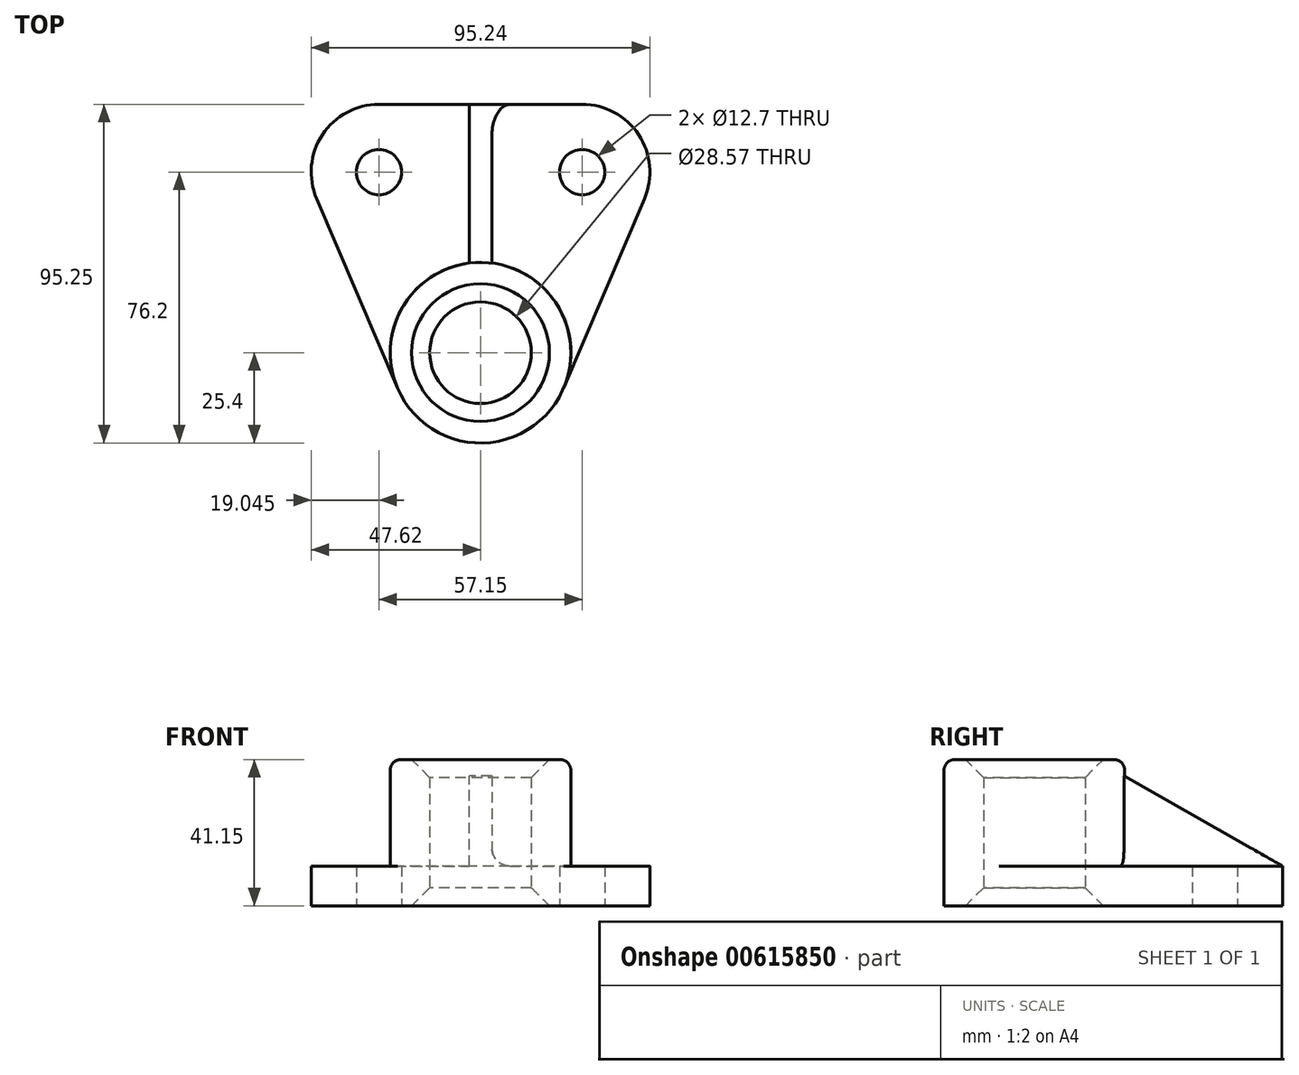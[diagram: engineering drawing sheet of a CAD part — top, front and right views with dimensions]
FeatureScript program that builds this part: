
annotation { "Feature Type Name" : "Feature", "Feature Type Description" : "" }
export const myFeature = defineFeature(function(context is Context, id is Id, definition is map)
    precondition{}
    {
        {
            var Q0;
            Q0=qCreatedBy(makeId("Top.planeOp"),FACE);
            var sketch = newSketch(context, id + "F0", { "sketchPlane" : qUnion([Q0])});
            skCircle(sketch, "E0", {"center": v(0, 0) * mm, "radius": 25.4 * mm});
            skLineSegment(sketch, "E1", {"start": v(0, 33.34) * mm, "end": v(0, -75.81) * mm, "construction": true});
            skCircle(sketch, "E2", {"center": v(0, 0) * mm, "radius": 14.29 * mm});
            skSolve(sketch);
        }
        {
            var Q0;
            Q0 = qSketchRegion(id + "F0", true);
            extrude(context, id + "F1", {"entities" : qUnion([Q0]), "depth" : 41.15 * mm, "offsetDistance" : 25.4 * mm});
        }
        {
            var Q0;
            Q0=makeQuery(id+"F1.opExtrude","CAP_FACE",FACE,{"disambiguationData":[OSD([sQuery(id+"F0.wireOp",EDGE,"E0"),sQuery(id+"F0.wireOp",EDGE,"E2")])],"isStart":true});
            var sketch = newSketch(context, id + "F2", { "sketchPlane" : qUnion([Q0])});
            skLineSegment(sketch, "E3", {"start": v(0, 41.82) * mm, "end": v(0, -91.73) * mm, "construction": true});
            skLineSegment(sketch, "E4", {"start": v(-52.73, -50.8) * mm, "end": v(63.33, -50.8) * mm, "construction": true});
            skArc(sketch, "E5", {"start": v(-46.1, -43.33) * mm, "mid": v(-44.47, -61.3) * mm, "end": v(-28.57, -69.85) * mm});
            skArc(sketch, "E6.MirrorC", {"start": v(46.1, -43.33) * mm, "mid": v(44.47, -61.3) * mm, "end": v(28.58, -69.85) * mm});
            skLineSegment(sketch, "E7", {"start": v(-52.6, 0) * mm, "end": v(62.29, 0) * mm, "construction": true});
            skCircle(sketch, "E8", {"center": v(-28.57, -50.8) * mm, "radius": 6.35 * mm});
            skCircle(sketch, "E9", {"center": v(28.58, -50.8) * mm, "radius": 6.35 * mm});
            skArc(sketch, "E10", {"start": v(-23.36, 9.97) * mm, "mid": v(0, -25.4) * mm, "end": v(23.36, 9.97) * mm});
            skLineSegment(sketch, "E11", {"start": v(-46.1, -43.33) * mm, "end": v(-23.36, 9.97) * mm});
            skLineSegment(sketch, "E12", {"start": v(23.36, 9.97) * mm, "end": v(46.1, -43.33) * mm});
            skLineSegment(sketch, "E13", {"start": v(-28.57, -69.85) * mm, "end": v(28.58, -69.85) * mm});
            skPoint(sketch, "E14.orphan", {"position": v(-52.73, -58.88) * mm});
            skSolve(sketch);
        }
        {
            var Q0;
            Q0 = qSketchRegion(id + "F2", true);
            extrude(context, id + "F3", {"entities" : qUnion([Q0]), "operationType" : NewBodyOperationType.ADD, "oppositeDirection" : true, "depth" : 11.18 * mm, "offsetDistance" : 25.4 * mm});
        }
        {
            var Q0;
            Q0=makeQuery(id+"F3.opExtrude","CAP_FACE",FACE,{"disambiguationData":[OSD([sQuery(id+"F2.wireOp",EDGE,"E5"),sQuery(id+"F2.wireOp",EDGE,"E6.MirrorC"),sQuery(id+"F2.wireOp",EDGE,"E8"),sQuery(id+"F2.wireOp",EDGE,"E9"),sQuery(id+"F2.wireOp",EDGE,"E10"),sQuery(id+"F2.wireOp",EDGE,"E11"),sQuery(id+"F2.wireOp",EDGE,"E12"),sQuery(id+"F2.wireOp",EDGE,"E13")])],"isStart":false});
            var sketch = newSketch(context, id + "F4", { "sketchPlane" : qUnion([Q0])});
            skLineSegment(sketch, "E15", {"start": v(0, 69.85) * mm, "end": v(0, 25.4) * mm, "construction": true});
            skLineSegment(sketch, "E16.bottom", {"start": v(-3.18, 69.85) * mm, "end": v(3.17, 69.85) * mm});
            skLineSegment(sketch, "E16.left", {"start": v(-3.18, 69.85) * mm, "end": v(-3.18, 25.2) * mm});
            skLineSegment(sketch, "E16.right", {"start": v(3.17, 69.85) * mm, "end": v(3.17, 25.2) * mm});
            skArc(sketch, "E17", {"start": v(3.17, 25.2) * mm, "mid": v(0, 25.4) * mm, "end": v(-3.18, 25.2) * mm});
            skSolve(sketch);
        }
        {
            var Q0;
            Q0 = qSketchRegion(id + "F4", true);
            extrude(context, id + "F5", {"entities" : qUnion([Q0]), "operationType" : NewBodyOperationType.ADD, "depth" : 25.4 * mm, "offsetDistance" : 25.4 * mm});
        }
        {
            var Q0;
            Q0=makeQuery(id+"F5.opExtrude","SWEPT_FACE",FACE,{"disambiguationData":[OSD([sQuery(id+"F4.wireOp",EDGE,"E16.left")])]});
            var sketch = newSketch(context, id + "F6", { "sketchPlane" : qUnion([Q0])});
            skLineSegment(sketch, "E18", {"start": v(-69.85, 11.18) * mm, "end": v(-25.2, 36.58) * mm});
            skLineSegment(sketch, "E19", {"start": v(-25.2, 36.58) * mm, "end": v(-69.85, 36.58) * mm});
            skLineSegment(sketch, "E20", {"start": v(-69.85, 36.58) * mm, "end": v(-69.85, 11.18) * mm});
            skSolve(sketch);
        }
        {
            var Q0;
            Q0 = qSketchRegion(id + "F6", true);
            extrude(context, id + "F7", {"entities" : qUnion([Q0]), "operationType" : NewBodyOperationType.REMOVE, "endBound" : BoundingType.UP_TO_NEXT, "oppositeDirection" : true, "depth" : 25.4 * mm, "offsetDistance" : 25.4 * mm});
        }
        {
            var Q0;
            {var subQ0=sQuery(id+"F2.wireOp",EDGE,"E11");var subQ1=sQuery(id+"F2.wireOp",EDGE,"E10");Q0=makeQuery(id+"F5.boolean.opBoolean","SPLIT",EDGE,{"disambiguationData":[TD([makeQuery(id+"F3.opExtrude","SWEPT_FACE",FACE,{"disambiguationData":[OSD([subQ0])]})])],"derivedFrom":makeQuery(id+"F3.opExtrude","CAP_EDGE",EDGE,{"disambiguationData":[OSD([subQ1])],"isStart":false})});}
            var Q1;
            Q1=makeQuery(id+"F5.opExtrude","CAP_EDGE",EDGE,{"disambiguationData":[OSD([sQuery(id+"F4.wireOp",EDGE,"E16.left")])],"isStart":true});
            var Q2;
            Q2=makeQuery(id+"F5.opExtrude","SWEPT_EDGE",EDGE,{"disambiguationData":[OSD([sQuery(id+"F2.wireOp",EDGE,"E10"),sQuery(id+"F4.wireOp",EDGE,"E16.left"),sQuery(id+"F4.wireOp",EDGE,"E17")])]});
            var Q3;
            Q3=makeQuery(id+"F5.opExtrude","SWEPT_EDGE",EDGE,{"disambiguationData":[OSD([sQuery(id+"F2.wireOp",EDGE,"E10"),sQuery(id+"F4.wireOp",EDGE,"E16.right"),sQuery(id+"F4.wireOp",EDGE,"E17")])]});
            var Q4;
            Q4=makeQuery(id+"F5.opExtrude","CAP_EDGE",EDGE,{"disambiguationData":[OSD([sQuery(id+"F4.wireOp",EDGE,"E16.right")])],"isStart":true});
            var Q5;
            {var subQ0=sQuery(id+"F2.wireOp",EDGE,"E12");var subQ1=sQuery(id+"F2.wireOp",EDGE,"E10");Q5=makeQuery(id+"F5.boolean.opBoolean","SPLIT",EDGE,{"disambiguationData":[TD([makeQuery(id+"F3.opExtrude","SWEPT_FACE",FACE,{"disambiguationData":[OSD([subQ0])]})])],"derivedFrom":makeQuery(id+"F3.opExtrude","CAP_EDGE",EDGE,{"disambiguationData":[OSD([subQ1])],"isStart":false})});}
            fillet(context, id + "F8", {"entities" : qUnion([Q0, Q1, Q2, Q3, Q4, Q5]), "radius" : 5.08 * mm, "tangentPropagation" : true, "allowEdgeOverflow" : false});
        }
        {
            var Q0;
            Q0=makeQuery(id+"F1.opExtrude","CAP_EDGE",EDGE,{"disambiguationData":[OSD([sQuery(id+"F0.wireOp",EDGE,"E0")])],"isStart":false});
            fillet(context, id + "F9", {"entities" : qUnion([Q0]), "radius" : 3.05 * mm, "tangentPropagation" : true, "allowEdgeOverflow" : false});
        }
        {
            var Q0;
            Q0=makeQuery(id+"F1.opExtrude","CAP_EDGE",EDGE,{"disambiguationData":[OSD([sQuery(id+"F0.wireOp",EDGE,"E2")])],"isStart":false});
            chamfer(context, id + "F10", {"entities" : qUnion([Q0]), "chamferType" : ChamferType.OFFSET_ANGLE, "width" : 5.08 * mm, "oppositeDirection" : false, "angle" : 45 * degree, "tangentPropagation" : true});
        }
        {
            var Q0;
            Q0=makeQuery(id+"F1.opExtrude","CAP_EDGE",EDGE,{"disambiguationData":[OSD([sQuery(id+"F0.wireOp",EDGE,"E2")])],"isStart":true});
            chamfer(context, id + "F11", {"entities" : qUnion([Q0]), "chamferType" : ChamferType.OFFSET_ANGLE, "width" : 5.08 * mm, "oppositeDirection" : false, "angle" : 45 * degree, "tangentPropagation" : true});
        }
    });
